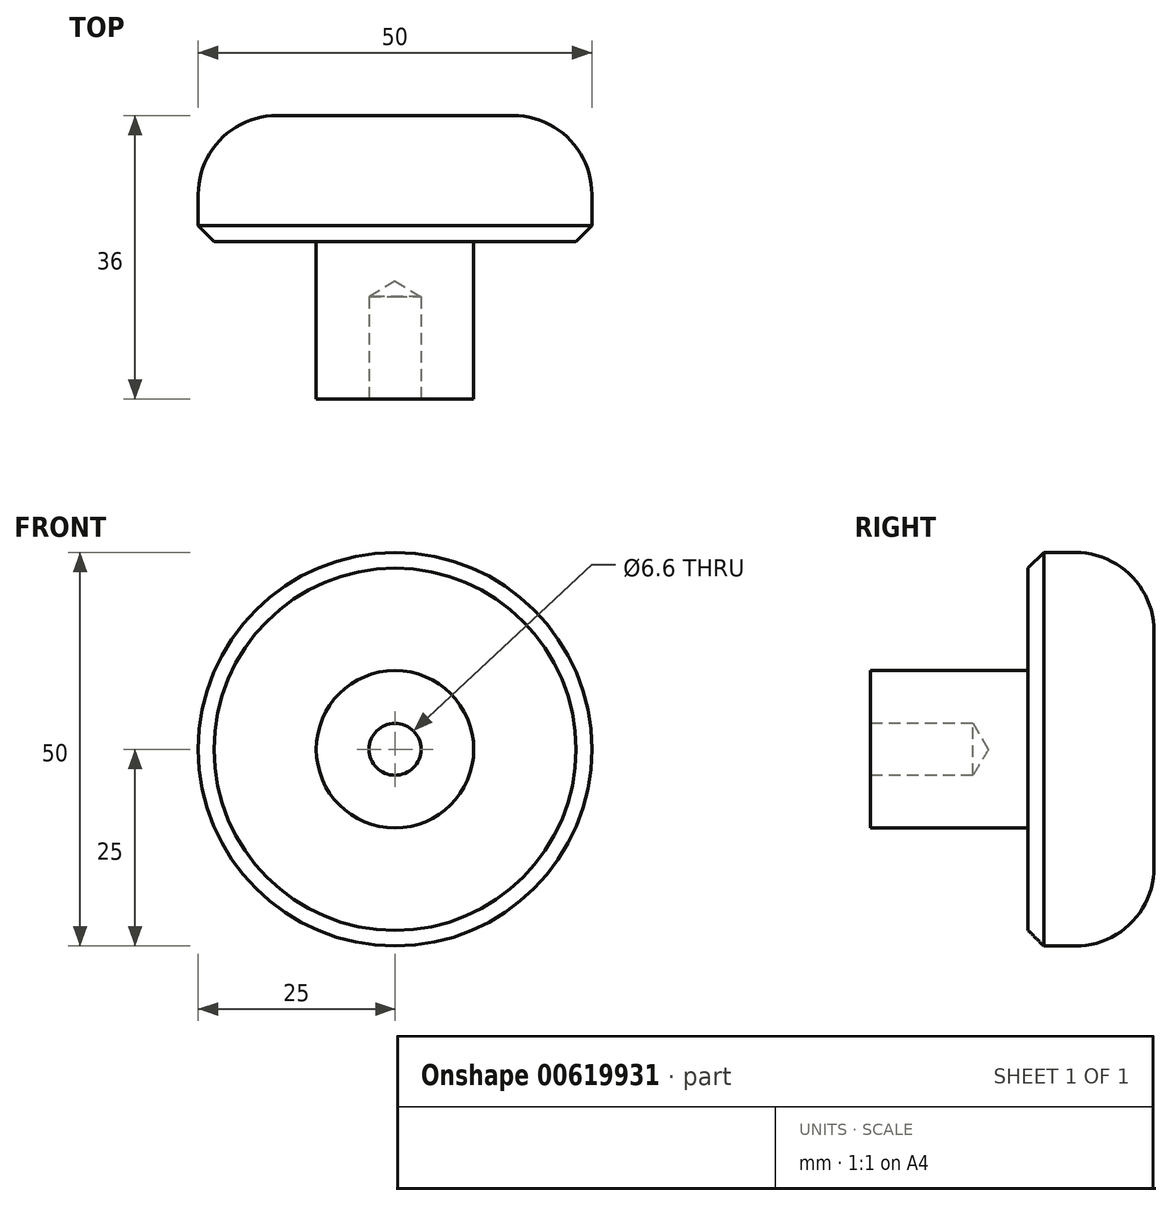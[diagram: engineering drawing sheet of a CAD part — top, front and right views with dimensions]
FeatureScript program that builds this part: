
annotation { "Feature Type Name" : "Feature", "Feature Type Description" : "" }
export const myFeature = defineFeature(function(context is Context, id is Id, definition is map)
    precondition{}
    {
        {
            var Q0;
            Q0=qCreatedBy(makeId("Front.planeOp"),FACE);
            var sketch = newSketch(context, id + "F0", { "sketchPlane" : qUnion([Q0])});
            skCircle(sketch, "E0", {"center": v(0, 0) * mm, "radius": 25 * mm});
            skSolve(sketch);
        }
        {
            var Q0;
            Q0=makeQuery(id+"F0.imprint","IMPRINT",FACE,{"disambiguationData":[TD([[makeQuery(id+"F0.imprint","IMPRINT",EDGE,{"derivedFrom":sQuery(id+"F0.wireOp",EDGE,"E0")}),1.0]])]});
            extrude(context, id + "F1", {"entities" : qUnion([Q0]), "depth" : 16 * mm, "offsetDistance" : 25 * mm});
        }
        {
            var Q0;
            Q0=makeQuery(id+"F1.opExtrude","CAP_FACE",FACE,{"disambiguationData":[OSD([sQuery(id+"F0.wireOp",EDGE,"E0")])],"isStart":false});
            var sketch = newSketch(context, id + "F2", { "sketchPlane" : qUnion([Q0])});
            skCircle(sketch, "E1", {"center": v(0, 0) * mm, "radius": 10 * mm});
            skSolve(sketch);
        }
        {
            var Q0;
            Q0=makeQuery(id+"F2.imprint","IMPRINT",FACE,{"disambiguationData":[TD([[makeQuery(id+"F2.imprint","IMPRINT",EDGE,{"derivedFrom":sQuery(id+"F2.wireOp",EDGE,"E1")}),1.0]])]});
            extrude(context, id + "F3", {"entities" : qUnion([Q0]), "operationType" : NewBodyOperationType.ADD, "depth" : 20 * mm, "offsetDistance" : 25 * mm});
        }
        {
            var Q0;
            Q0=makeQuery(id+"F1.opExtrude","CAP_EDGE",EDGE,{"disambiguationData":[OSD([sQuery(id+"F0.wireOp",EDGE,"E0")])],"isStart":true});
            fillet(context, id + "F4", {"entities" : qUnion([Q0]), "radius" : 10 * mm, "tangentPropagation" : true, "allowEdgeOverflow" : false});
        }
        {
            var Q0;
            Q0=makeQuery(id+"F1.opExtrude","CAP_EDGE",EDGE,{"disambiguationData":[OSD([sQuery(id+"F0.wireOp",EDGE,"E0")])],"isStart":false});
            chamfer(context, id + "F5", {"entities" : qUnion([Q0]), "width" : 2 * mm, "tangentPropagation" : true});
        }
        {
            var Q0;
            Q0=makeQuery(id+"F3.opExtrude","CAP_FACE",FACE,{"disambiguationData":[OSD([sQuery(id+"F2.wireOp",EDGE,"E1")])],"isStart":false});
            var sketch = newSketch(context, id + "F6", { "sketchPlane" : qUnion([Q0])});
            skCircle(sketch, "E2", {"center": v(0, 0) * mm, "radius": 3 * mm});
            skSolve(sketch);
        }
        {
            var Q0;
            Q0=sQuery(id+"F6.wireOp",VERTEX,"E2.center");
            var Q1;
            Q1=makeQuery(id+"F1.opExtrude","SWEPT_BODY",BODY,{"disambiguationData":[OSD([sQuery(id+"F0.wireOp",EDGE,"E0")])]});
            hole(context, id + "F7", {"style" : HoleStyle.SIMPLE, "endStyle" : HoleEndStyle.BLIND, "holeDiameter" : 6.6 * mm, "majorDiameter" : 5 * mm, "holeDepth" : 13 * mm, "isTappedThrough" : true, "tappedDepth" : 12 * mm, "tapClearance" : 3, "startFromSketch" : true, "locations" : qUnion([Q0]), "scope" : qUnion([Q1])});
        }
    });
